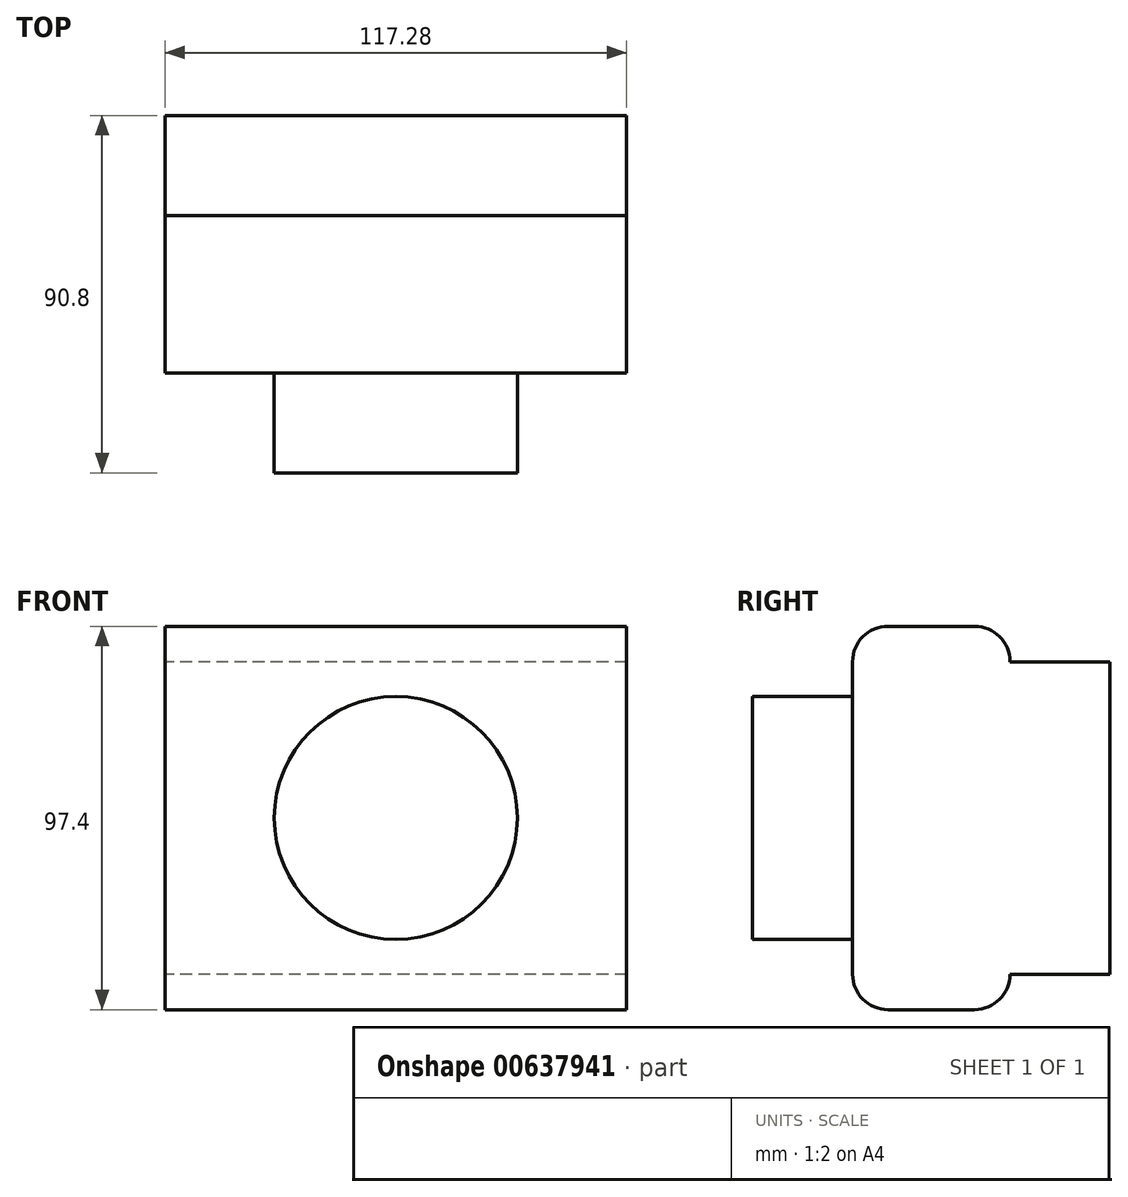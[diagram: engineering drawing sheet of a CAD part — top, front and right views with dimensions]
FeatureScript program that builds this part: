
annotation { "Feature Type Name" : "Feature", "Feature Type Description" : "" }
export const myFeature = defineFeature(function(context is Context, id is Id, definition is map)
    precondition{}
    {
        {
            var Q0;
            Q0=qCreatedBy(makeId("Front.planeOp"),FACE);
            var sketch = newSketch(context, id + "F0", { "sketchPlane" : qUnion([Q0])});
            skLineSegment(sketch, "E0.bottom", {"start": v(58.64, 48.7) * mm, "end": v(-58.64, 48.7) * mm});
            skLineSegment(sketch, "E0.top", {"start": v(58.64, -48.7) * mm, "end": v(-58.64, -48.7) * mm});
            skLineSegment(sketch, "E0.left", {"start": v(58.64, 48.7) * mm, "end": v(58.64, -48.7) * mm});
            skLineSegment(sketch, "E0.right", {"start": v(-58.64, 48.7) * mm, "end": v(-58.64, -48.7) * mm});
            skPoint(sketch, "E0.middle", {"position": v(0, 0) * mm});
            skSolve(sketch);
        }
        {
            var Q0;
            Q0=makeQuery(id+"F0.imprint","IMPRINT",FACE,{"disambiguationData":[TD([[makeQuery(id+"F0.imprint","IMPRINT",EDGE,{"derivedFrom":sQuery(id+"F0.wireOp",EDGE,"E0.bottom")}),1.0]])]});
            extrude(context, id + "F1", {"entities" : qUnion([Q0]), "depth" : 40 * mm, "offsetDistance" : 25.4 * mm});
        }
        {
            var Q0;
            Q0=makeQuery(id+"F1.opExtrude","CAP_EDGE",EDGE,{"disambiguationData":[OSD([sQuery(id+"F0.wireOp",EDGE,"E0.bottom")])],"isStart":true});
            var Q1;
            Q1=makeQuery(id+"F1.opExtrude","CAP_EDGE",EDGE,{"disambiguationData":[OSD([sQuery(id+"F0.wireOp",EDGE,"E0.bottom")])],"isStart":false});
            var Q2;
            Q2=makeQuery(id+"F1.opExtrude","CAP_EDGE",EDGE,{"disambiguationData":[OSD([sQuery(id+"F0.wireOp",EDGE,"E0.top")])],"isStart":false});
            var Q3;
            Q3=makeQuery(id+"F1.opExtrude","CAP_EDGE",EDGE,{"disambiguationData":[OSD([sQuery(id+"F0.wireOp",EDGE,"E0.top")])],"isStart":true});
            fillet(context, id + "F2", {"entities" : qUnion([Q0, Q1, Q2, Q3]), "radius" : 9 * mm, "tangentPropagation" : true, "allowEdgeOverflow" : false});
        }
        {
            var Q0;
            Q0=makeQuery(id+"F1.opExtrude","CAP_FACE",FACE,{"disambiguationData":[OSD([sQuery(id+"F0.wireOp",EDGE,"E0.bottom"),sQuery(id+"F0.wireOp",EDGE,"E0.top"),sQuery(id+"F0.wireOp",EDGE,"E0.left"),sQuery(id+"F0.wireOp",EDGE,"E0.right")])],"isStart":false});
            var sketch = newSketch(context, id + "F3", { "sketchPlane" : qUnion([Q0])});
            skSolve(sketch);
        }
        {
            var Q0;
            {var subQ1=sQuery(id+"F0.wireOp",EDGE,"E0.left");Q0=makeQuery(id+"F3.imprint","IMPRINT",FACE,{"disambiguationData":[TD([[makeQuery(id+"F3.imprint","IMPRINT",EDGE,{"derivedFrom":makeQuery(id+"F1.opExtrude","CAP_EDGE",EDGE,{"disambiguationData":[OSD([subQ1])],"isStart":false})}),-1.0]])]});}
            var sketch = newSketch(context, id + "F4", { "sketchPlane" : qUnion([Q0])});
            skCircle(sketch, "E1", {"center": v(0, 0) * mm, "radius": 30.88 * mm});
            skSolve(sketch);
        }
        {
            var Q0;
            Q0=makeQuery(id+"F4.imprint","IMPRINT",FACE,{"disambiguationData":[TD([[makeQuery(id+"F4.imprint","IMPRINT",EDGE,{"derivedFrom":sQuery(id+"F4.wireOp",EDGE,"E1")}),1.0]])]});
            extrude(context, id + "F5", {"entities" : qUnion([Q0]), "operationType" : NewBodyOperationType.ADD, "depth" : 25.4 * mm, "offsetDistance" : 25.4 * mm});
        }
        {
            var Q0;
            Q0=makeQuery(id+"F1.opExtrude","CAP_FACE",FACE,{"disambiguationData":[OSD([sQuery(id+"F0.wireOp",EDGE,"E0.bottom"),sQuery(id+"F0.wireOp",EDGE,"E0.top"),sQuery(id+"F0.wireOp",EDGE,"E0.left"),sQuery(id+"F0.wireOp",EDGE,"E0.right")])],"isStart":true});
            extrude(context, id + "F6", {"entities" : qUnion([Q0]), "operationType" : NewBodyOperationType.ADD, "depth" : 25.4 * mm, "offsetDistance" : 25.4 * mm});
        }
    });
